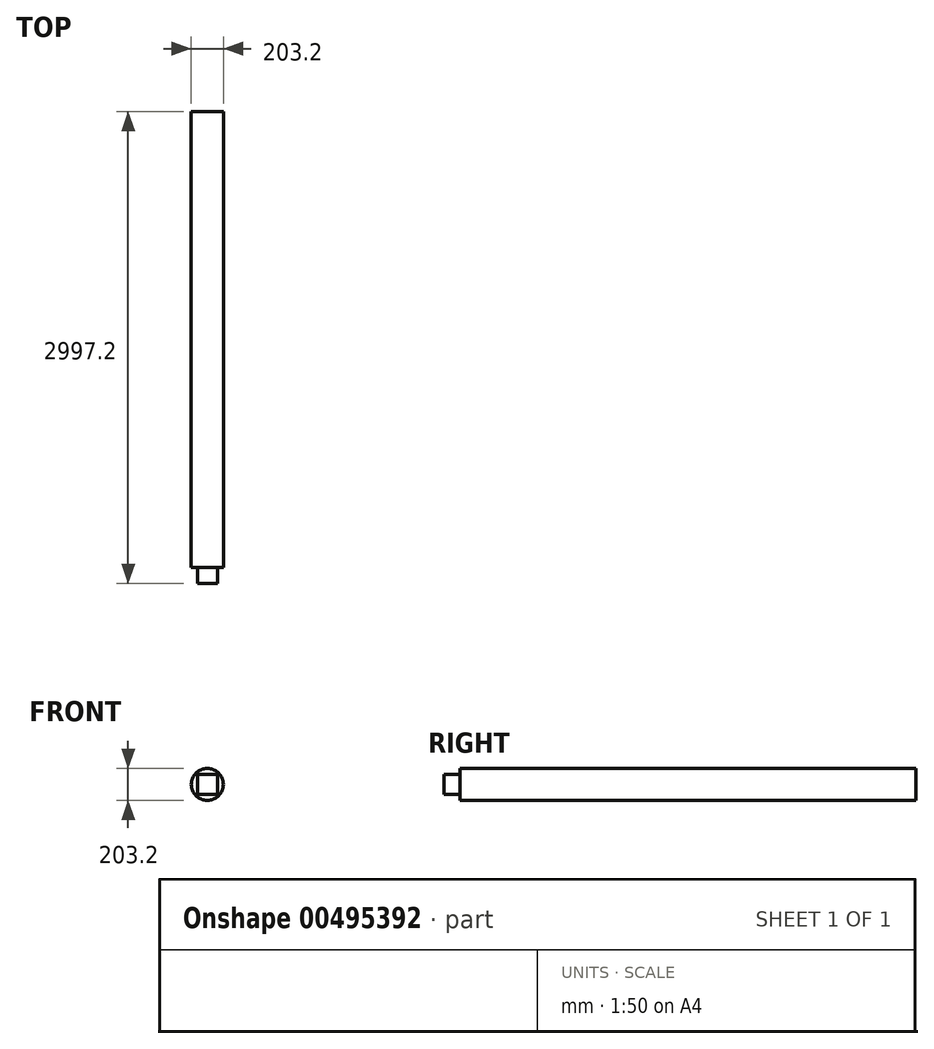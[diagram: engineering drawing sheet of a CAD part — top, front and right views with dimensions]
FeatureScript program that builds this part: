
annotation { "Feature Type Name" : "Feature", "Feature Type Description" : "" }
export const myFeature = defineFeature(function(context is Context, id is Id, definition is map)
    precondition{}
    {
        {
            var Q0;
            Q0=qCreatedBy(makeId("Front.planeOp"),FACE);
            var sketch = newSketch(context, id + "F0", { "sketchPlane" : qUnion([Q0])});
            skCircle(sketch, "E0", {"center": v(0, 0) * mm, "radius": 101.6 * mm});
            skSolve(sketch);
        }
        {
            var Q0;
            Q0 = qSketchRegion(id + "F0", true);
            extrude(context, id + "F1", {"entities" : qUnion([Q0]), "depth" : 2895.6 * mm, "offsetDistance" : 25.4 * mm});
        }
        {
            var Q0;
            Q0=makeQuery(id+"F1.opExtrude","CAP_FACE",FACE,{"disambiguationData":[OSD([sQuery(id+"F0.wireOp",EDGE,"E0")])],"isStart":false});
            var sketch = newSketch(context, id + "F2", { "sketchPlane" : qUnion([Q0])});
            skLineSegment(sketch, "E1.bottom", {"start": v(-63.5, 63.5) * mm, "end": v(63.5, 63.5) * mm});
            skLineSegment(sketch, "E1.top", {"start": v(-63.5, -63.5) * mm, "end": v(63.5, -63.5) * mm});
            skLineSegment(sketch, "E1.left", {"start": v(-63.5, 63.5) * mm, "end": v(-63.5, -63.5) * mm});
            skLineSegment(sketch, "E1.right", {"start": v(63.5, 63.5) * mm, "end": v(63.5, -63.5) * mm});
            skSolve(sketch);
        }
        {
            var Q0;
            Q0 = qSketchRegion(id + "F2", true);
            extrude(context, id + "F3", {"entities" : qUnion([Q0]), "operationType" : NewBodyOperationType.ADD, "depth" : 101.6 * mm, "offsetDistance" : 25.4 * mm});
        }
    });
